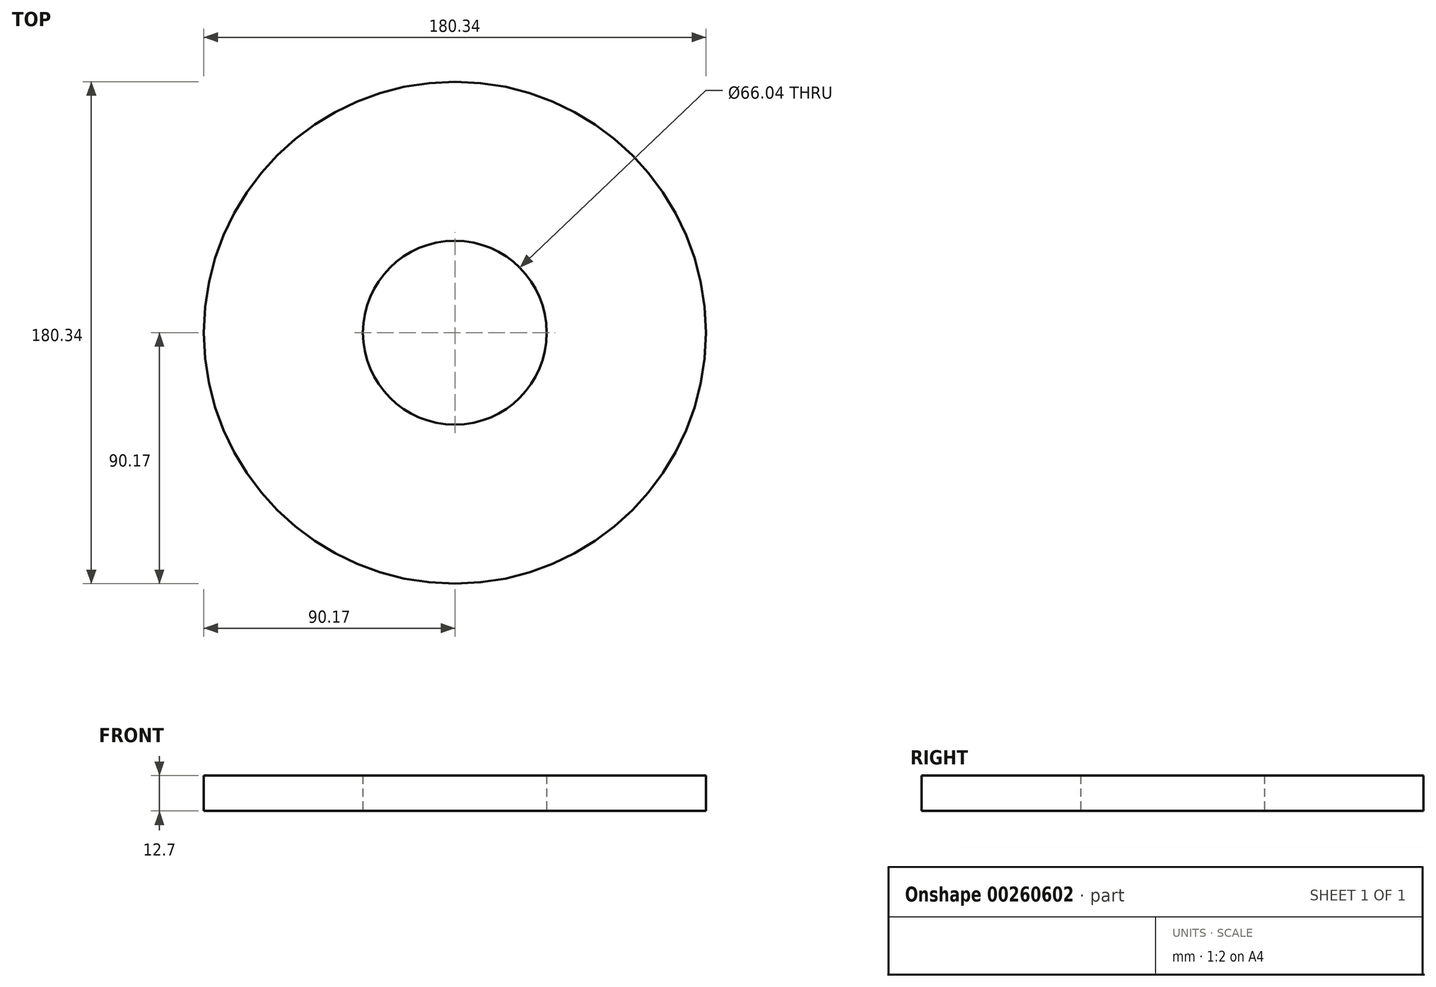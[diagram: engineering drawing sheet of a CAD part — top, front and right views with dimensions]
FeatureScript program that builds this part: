
annotation { "Feature Type Name" : "Feature", "Feature Type Description" : "" }
export const myFeature = defineFeature(function(context is Context, id is Id, definition is map)
    precondition{}
    {
        {
            var Q0;
            Q0=qCreatedBy(makeId("Top.planeOp"),FACE);
            var sketch = newSketch(context, id + "F0", { "sketchPlane" : qUnion([Q0])});
            skCircle(sketch, "E0", {"center": v(0, 0) * mm, "radius": 90.17 * mm});
            skCircle(sketch, "E1", {"center": v(0, 0) * mm, "radius": 33.02 * mm});
            skSolve(sketch);
        }
        {
            var Q0;
            Q0=makeQuery(id+"F0.imprint","IMPRINT",FACE,{"disambiguationData":[TD([[makeQuery(id+"F0.imprint","IMPRINT",EDGE,{"derivedFrom":sQuery(id+"F0.wireOp",EDGE,"E0")}),1.0]])]});
            extrude(context, id + "F1", {"entities" : qUnion([Q0]), "depth" : 12.7 * mm});
        }
    });
